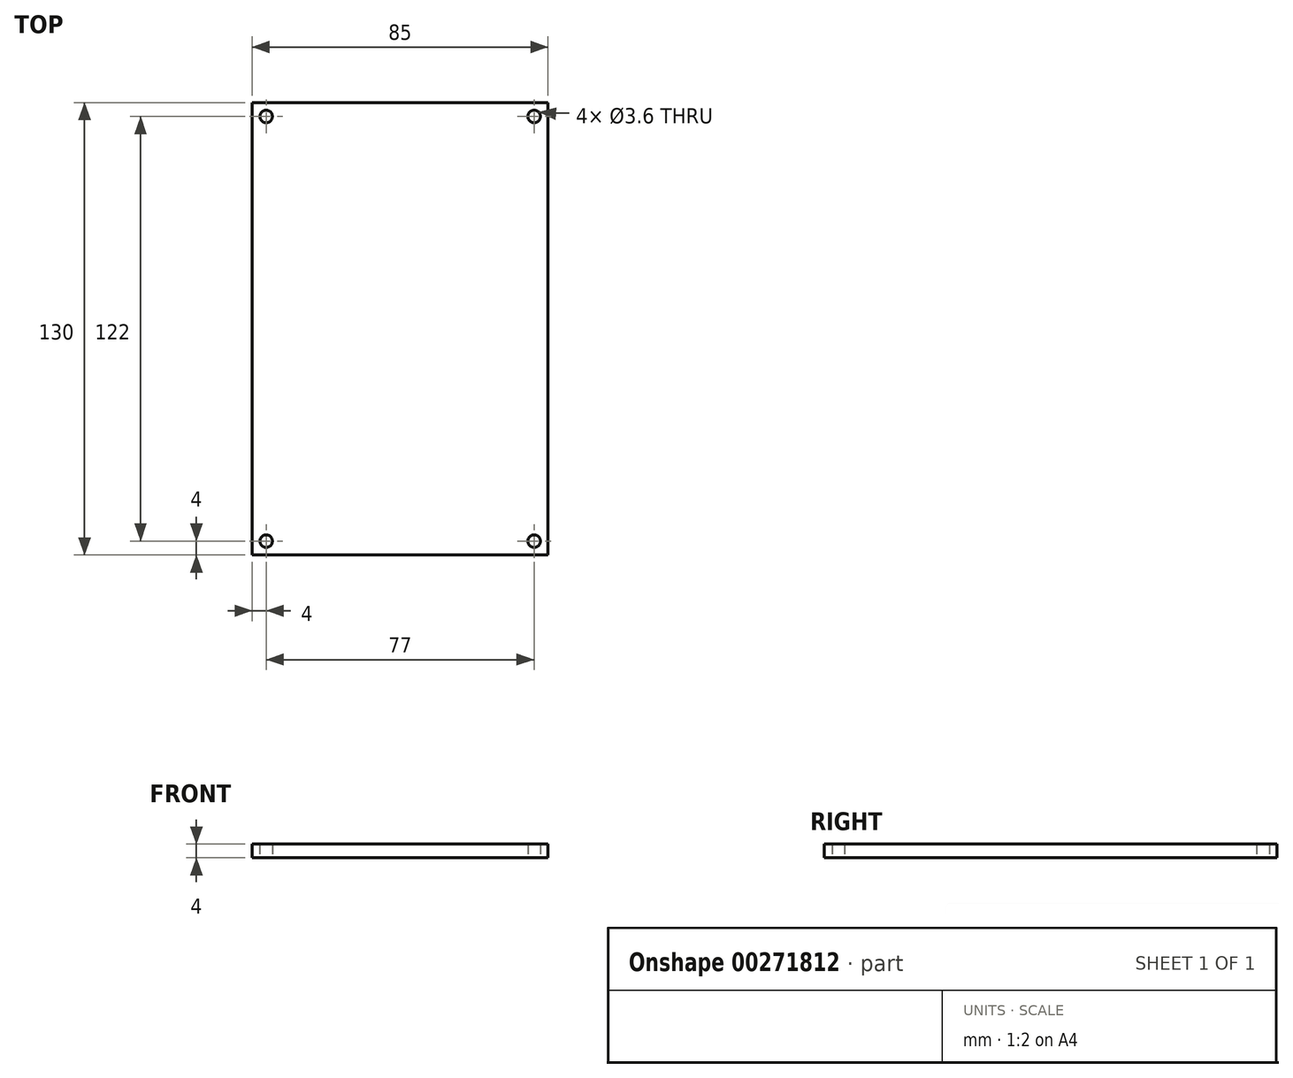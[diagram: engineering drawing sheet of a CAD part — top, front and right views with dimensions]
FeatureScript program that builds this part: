
annotation { "Feature Type Name" : "Feature", "Feature Type Description" : "" }
export const myFeature = defineFeature(function(context is Context, id is Id, definition is map)
    precondition{}
    {
        {
            assignVariable(context, id + "F0", {"name" : "HoleDiameter", "anyValue" : 3.6});
        }
        {
            assignVariable(context, id + "F1", {"name" : "PCB_Thickness", "anyValue" : 4});
        }
        {
            var Q0;
            Q0=qCreatedBy(makeId("Top.planeOp"),FACE);
            var sketch = newSketch(context, id + "F2", { "sketchPlane" : qUnion([Q0])});
            skLineSegment(sketch, "E0.bottom", {"start": v(42.5, 65) * mm, "end": v(-42.5, 65) * mm});
            skLineSegment(sketch, "E0.top", {"start": v(42.5, -65) * mm, "end": v(-42.5, -65) * mm});
            skLineSegment(sketch, "E0.left", {"start": v(42.5, 65) * mm, "end": v(42.5, -65) * mm});
            skLineSegment(sketch, "E0.right", {"start": v(-42.5, 65) * mm, "end": v(-42.5, -65) * mm});
            skPoint(sketch, "E0.middle", {"position": v(0, 0) * mm});
            skLineSegment(sketch, "E1", {"start": v(0, -65) * mm, "end": v(0, 65) * mm, "construction": true});
            skLineSegment(sketch, "E2", {"start": v(-42.5, 0) * mm, "end": v(42.5, 0) * mm, "construction": true});
            skPoint(sketch, "E3", {"position": v(-38.5, 61) * mm});
            skPoint(sketch, "E4", {"position": v(38.5, 61) * mm});
            skPoint(sketch, "E5", {"position": v(-38.5, -61) * mm});
            skPoint(sketch, "E6", {"position": v(38.5, -61) * mm});
            skSolve(sketch);
        }
        {
            var Q0;
            Q0=qSketchRegion(id+"F2",true);
            extrude(context, id + "F3", {"entities" : qUnion([Q0]), "depth" : (getVariable(context, 'PCB_Thickness')) * mm});
        }
        {
            var Q0;
            Q0=sQuery(id+"F2.wireOp",VERTEX,"E4");
            var Q1;
            Q1=sQuery(id+"F2.wireOp",VERTEX,"E6");
            var Q2;
            Q2=sQuery(id+"F2.wireOp",VERTEX,"E5");
            var Q3;
            Q3=sQuery(id+"F2.wireOp",VERTEX,"E3");
            var Q4;
            Q4=makeQuery(id+"F3.opExtrude","SWEPT_BODY",BODY,{"disambiguationData":[OSD([sQuery(id+"F2.wireOp",EDGE,"E0.bottom"),sQuery(id+"F2.wireOp",EDGE,"E0.top"),sQuery(id+"F2.wireOp",EDGE,"E0.left"),sQuery(id+"F2.wireOp",EDGE,"E0.right")])]});
            hole(context, id + "F4", {"style" : HoleStyle.SIMPLE, "endStyle" : HoleEndStyle.BLIND, "oppositeDirection" : true, "holeDiameter" : (getVariable(context, 'HoleDiameter')) * mm, "holeDepth" : (getVariable(context, 'PCB_Thickness')) * mm, "startFromSketch" : true, "locations" : qUnion([Q0, Q1, Q2, Q3]), "scope" : qUnion([Q4])});
        }
        {
            assignVariable(context, id + "F5", {"name" : "Case_Spacers", "anyValue" : 5});
        }
        {
            var Q0;
            Q0=qCreatedBy(makeId("Top.planeOp"),FACE);
            cPlane(context, id + "F6", {"entities" : qUnion([Q0]), "cplaneType" : CPlaneType.OFFSET, "offset" : (getVariable(context, 'Case_Spacers')) * mm, "oppositeDirection" : true, "width" : 150 * mm, "height" : 150 * mm});
        }
    });
